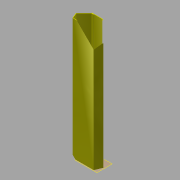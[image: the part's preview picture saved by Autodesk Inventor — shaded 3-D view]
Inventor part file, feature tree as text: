
AUTODESK INVENTOR PART (.ipt)
format: ipt  version: 2014 (Build 180170000, 170)  size: 133,120 bytes
history: native  units: mm
features: reference x3, extrude x2, fillet x2, sketch x2, plane x1, chamfer x1, projected_geometry x1
ambient origin geometry x8: Origin, YZ Plane, XZ Plane, XY Plane, X Axis, Y Axis, Z Axis, Center Point
bodies: Solid1 (feature_tree)
feature tree (12):
  extrude  "Extrusion1"  Depth=20.0mm
  plane  "Work Plane1"
  extrude  "Extrusion2"  Depth=1000.0mm TaperAngle=0.0deg
  fillet  "Fillet1"  Radius=4.0mm
  fillet  "Fillet2"  Radius=1000.0mm
  chamfer  "Chamfer1"  Distance=6.0mm
  sketch  "Sketch1"  dims[d1=20.0mm d2=20.0mm]
  reference  "Reference1"
  sketch  "Sketch2"  dims[d3=4.0mm d4=1000.0mm d5=0.0mm d6=4.0mm d7=1000.0mm d8=0.0mm d9=6.0mm d10=6.0mm d11=1.0mm d12=2.0mm d13=45.0deg]
  reference  "Reference2"
  reference  "Reference3"
  projected_geometry  "Projected Loop1"
